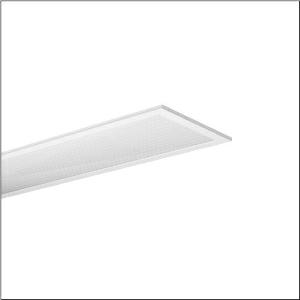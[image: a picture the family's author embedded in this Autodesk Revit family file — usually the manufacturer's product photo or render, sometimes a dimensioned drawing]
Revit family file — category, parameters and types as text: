
# Revit family: apollon_r__21_linear_51mq17wd2412_9bf3
name_source: partatom
category: Lighting Fixtures
units: mm (PartAtom-declared; Revit-internal decimal feet)

## family parameters
Cut with Voids When Loaded = No
Host = Face
Light Source = No
Part Type = Normal
Room Calculation Point = No
Round Connector Dimension = Use Diameter
Shared = No

## types (1)
- Apollon® 21 linear (1 x LED, 7200 lm, 60 W, 4000K)
    Apparent Load = 60 VA
    CIE Flux Codes = 61 87 97 100 100
    Color Rendering = 80
    Color Temperature = 4000K
    Default Elevation = 1800 mm
    Description = Apollon® 21 linear, office luminaire, primary optical cover: micro prismatic cover, CAT 2 (L<= 3000cd/m²), light emission: direct distribution, primary light characteristic: symmetric, installation type: lay-in mounting, LED, rated luminous flux: 7.200lm, luminous efficacy: 120lm/W, light colour: 840, colour temperature: 4000K, control gear: ECG DALI, with terminal, 5-pole, mains connection: 220..240V, AC, 50/60Hz, rated input power: 60W, housing, of aluminium, coated, pure white, length: 1.545mm, width: 307mm, height: 48mm, housing upper side, of sheet steel, galvanised, protection rating (complete): IP20, protection rating (lamp compartment, on room side): IP50, insulation class (complete): insulation class I (protective earthing), certification: CE, ENEC, packaging unit: 1 piece
    Height = 0 mm  [stored 0 ft]
    Lamp = 1 x LED
    Lamp Light Flux = 7200 lm
    Lamp Power = 60 W
    Lamp count = 1
    Length = 1545 mm
    Luminous efficacy = 120 lm/W
    Manufacturer = Siteco
    ModVariant = No
    Model = 51MQ17WD2412
    Mounting Place = Ceiling
    Mounting Type = Recessed
    Number of Poles = 1
    OnlyDefault = Yes
    Power Factor = 1
    Product Name = Apollon® 21 linear
    Product group = office luminaire | ceiling recessed
    ProductGroupID = 401
    Protection Class = Protection class I
    Protection Degree = IP 20
    RLX_Detail_Level = 1
    RLX_Emergency_Light_Flux = 0 lm
    RLX_Emergency_Type = 0
    RLX_Emergency_Type_DB = No
    RlxData = <blob elided: 17261 chars, md5=42c876ee>
    Socket = socket
    Standby Power = 0 W
    System Light Flux = 7200 lm
    System Power = 60 W
    Type Comments = Product without accessories
    Type Image = l_1291045.jpg
    URL = http://relux.com
    VarID = ---
    Voltage = 0 V
    Weight = 0.00 kg
    Width = 307 mm

note: [stored X ft] marks values corroborated as IEEE doubles in the binary element streams (Revit-internal decimal feet)

## geometry (parser evidence)
native form markers: Blend x4, Sweep x11
no freeform markers — native parametric forms only
